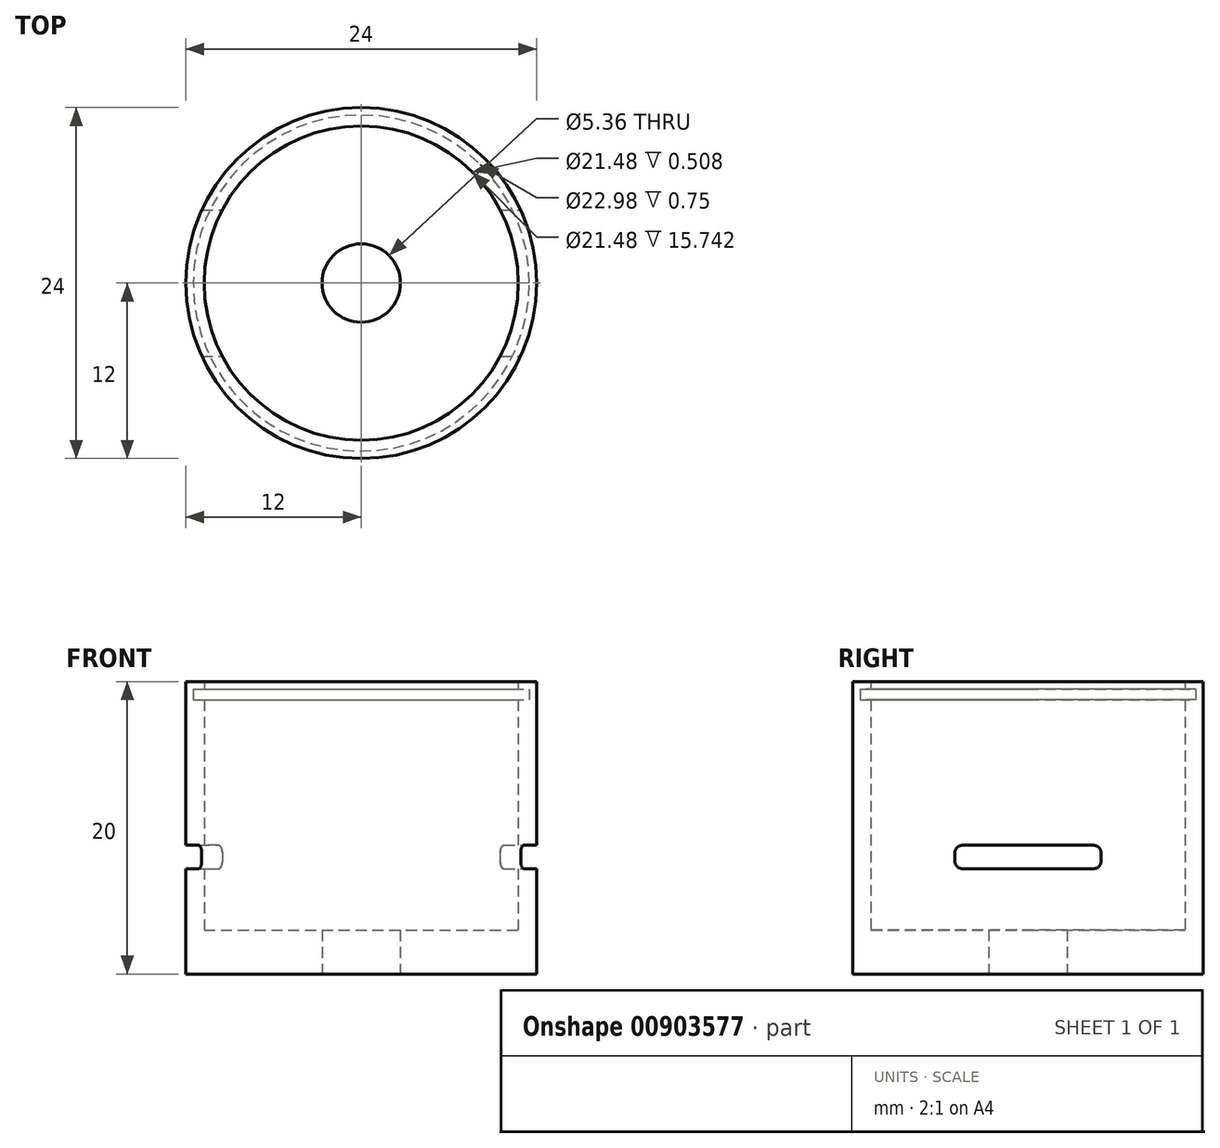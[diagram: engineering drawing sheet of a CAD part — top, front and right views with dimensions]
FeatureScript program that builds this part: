
annotation { "Feature Type Name" : "Feature", "Feature Type Description" : "" }
export const myFeature = defineFeature(function(context is Context, id is Id, definition is map)
    precondition{}
    {
        {
            var Q0;
            Q0=qCreatedBy(makeId("Front.planeOp"),FACE);
            var sketch = newSketch(context, id + "F0", { "sketchPlane" : qUnion([Q0])});
            skLineSegment(sketch, "E0", {"start": v(2.68, 0) * mm, "end": v(12, 0) * mm});
            skLineSegment(sketch, "E1", {"start": v(12, 0) * mm, "end": v(12, 20) * mm});
            skLineSegment(sketch, "E2", {"start": v(12, 20) * mm, "end": v(10.74, 20) * mm});
            skLineSegment(sketch, "E3", {"start": v(10.74, 20) * mm, "end": v(10.74, 19.5) * mm});
            skLineSegment(sketch, "E4", {"start": v(10.74, 19.5) * mm, "end": v(11.5, 19.5) * mm});
            skLineSegment(sketch, "E5", {"start": v(11.5, 19.5) * mm, "end": v(11.5, 18.74) * mm});
            skLineSegment(sketch, "E6", {"start": v(11.5, 18.74) * mm, "end": v(10.74, 18.74) * mm});
            skLineSegment(sketch, "E7", {"start": v(10.74, 18.74) * mm, "end": v(10.74, 3) * mm});
            skLineSegment(sketch, "E8", {"start": v(10.74, 3) * mm, "end": v(2.68, 3) * mm});
            skLineSegment(sketch, "E9", {"start": v(2.68, 3) * mm, "end": v(2.68, 0) * mm});
            skLineSegment(sketch, "E10", {"start": v(0, 0) * mm, "end": v(0, 15.08) * mm, "construction": true});
            skSolve(sketch);
        }
        {
            var Q0;
            Q0 = qSketchRegion(id + "F0", true);
            var Q1;
            Q1=sQuery(id+"F0.wireOp",EDGE,"E10");
            revolve(context, id + "F1", {"surfaceOperationType" : NewSurfaceOperationType.NEW, "entities" : qUnion([Q0]), "axis" : qUnion([Q1]), "revolveType" : RevolveType.FULL});
        }
        {
            var Q0;
            Q0=qCreatedBy(makeId("Right.planeOp"),FACE);
            var sketch = newSketch(context, id + "F2", { "sketchPlane" : qUnion([Q0])});
            skCircle(sketch, "E11", {"center": v(0, 8) * mm, "radius": 1.5 * mm, "construction": true});
            skLineSegment(sketch, "E12.bottom", {"start": v(4.5, 8.8) * mm, "end": v(-4.5, 8.8) * mm});
            skLineSegment(sketch, "E12.top", {"start": v(4.5, 7.2) * mm, "end": v(-4.5, 7.2) * mm});
            skLineSegment(sketch, "E12.left", {"start": v(5, 8.3) * mm, "end": v(5, 7.7) * mm});
            skLineSegment(sketch, "E12.right", {"start": v(-5, 8.3) * mm, "end": v(-5, 7.7) * mm});
            skPoint(sketch, "E13.visualSharp", {"position": v(-5, 8.8) * mm});
            skArc(sketch, "E13.filletArc", {"start": v(-4.5, 8.8) * mm, "mid": v(-4.85, 8.65) * mm, "end": v(-5, 8.3) * mm});
            skPoint(sketch, "E14.visualSharp", {"position": v(-5, 7.2) * mm});
            skArc(sketch, "E14.filletArc", {"start": v(-5, 7.7) * mm, "mid": v(-4.85, 7.35) * mm, "end": v(-4.5, 7.2) * mm});
            skPoint(sketch, "E15.visualSharp", {"position": v(5, 7.2) * mm});
            skArc(sketch, "E15.filletArc", {"start": v(4.5, 7.2) * mm, "mid": v(4.85, 7.35) * mm, "end": v(5, 7.7) * mm});
            skPoint(sketch, "E16.visualSharp", {"position": v(5, 8.8) * mm});
            skArc(sketch, "E16.filletArc", {"start": v(5, 8.3) * mm, "mid": v(4.85, 8.65) * mm, "end": v(4.5, 8.8) * mm});
            skSolve(sketch);
        }
        {
            var Q0;
            Q0 = qSketchRegion(id + "F2", true);
            extrude(context, id + "F3", {"entities" : qUnion([Q0]), "operationType" : NewBodyOperationType.REMOVE, "endBound" : BoundingType.THROUGH_ALL, "oppositeDirection" : true, "depth" : 25 * mm, "offsetDistance" : 25 * mm, "hasSecondDirection" : true, "secondDirectionBound" : SecondDirectionBoundingType.THROUGH_ALL, "secondDirectionOppositeDirection" : false, "secondDirectionDepth" : 25 * mm});
        }
    });
